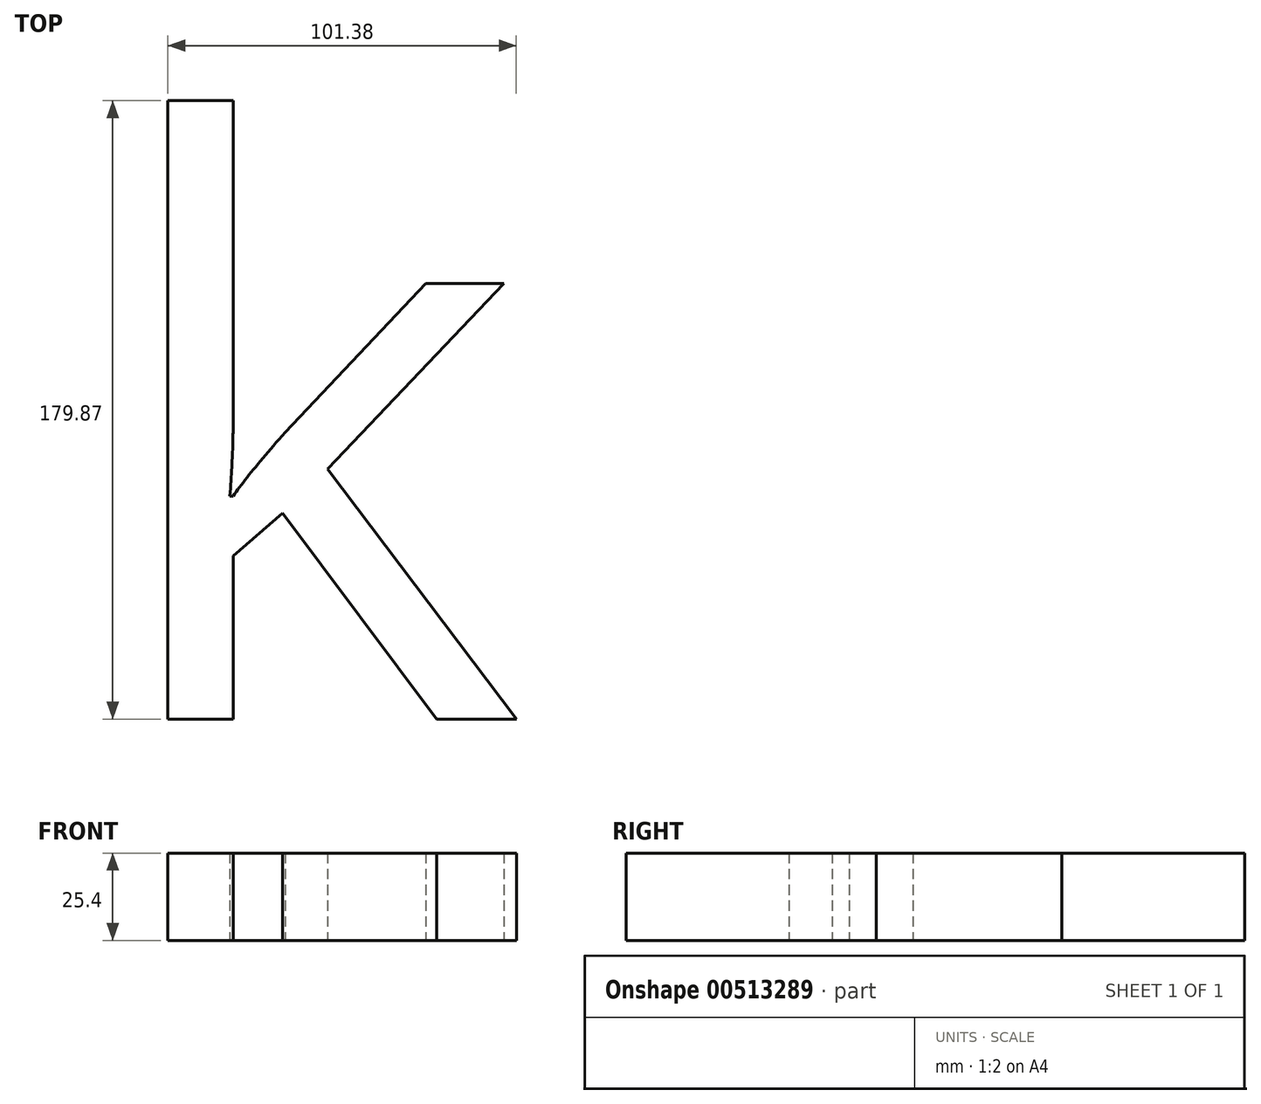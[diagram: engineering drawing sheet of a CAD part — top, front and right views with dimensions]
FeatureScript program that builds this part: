
annotation { "Feature Type Name" : "Feature", "Feature Type Description" : "" }
export const myFeature = defineFeature(function(context is Context, id is Id, definition is map)
    precondition{}
    {
        {
            var Q0;
            Q0=qCreatedBy(makeId("Top.planeOp"),FACE);
            var sketch = newSketch(context, id + "F0", { "sketchPlane" : qUnion([Q0])});
            skText(sketch, "E0", { "text": "there it is....bam.....oh shit..now we are cooking!\nyes....are you ready for this", "fontName": "OpenSans-Regular.ttf"});
            const initialGuessF0  = {"E0": [-5.2251, -0.20405, 1, 0, 0.17044]};
            skSetInitialGuess(sketch, initialGuessF0);
            skSolve(sketch);
        }
        {
            var Q0;
            Q0=makeQuery(id+"F0.imprint","IMPRINT",FACE,{"disambiguationData":[TD([[makeQuery(id+"F0.imprint","IMPRINT",EDGE,{"derivedFrom":sQuery(id+"F0.wireOp",EDGE,"E0.sketch_text.stroke-638")}),-1.0]])]});
            extrude(context, id + "F1", {"entities" : qUnion([Q0]), "depth" : 25.4 * mm});
        }
    });
